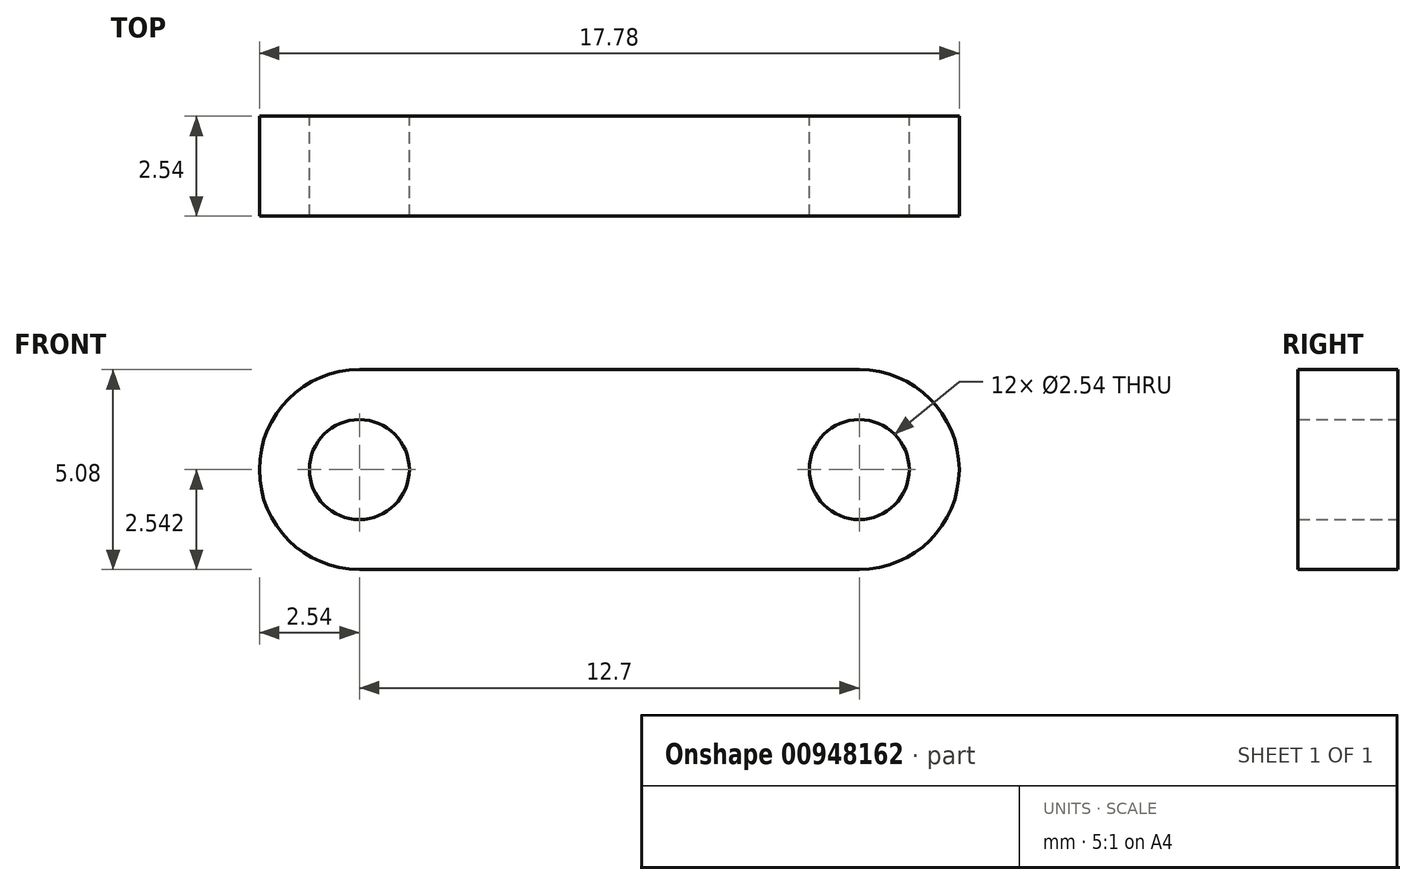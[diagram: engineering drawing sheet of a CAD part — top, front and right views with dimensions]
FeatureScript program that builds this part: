
annotation { "Feature Type Name" : "Feature", "Feature Type Description" : "" }
export const myFeature = defineFeature(function(context is Context, id is Id, definition is map)
    precondition{}
    {
        {
            var Q0;
            Q0=qCreatedBy(makeId("Front.planeOp"),FACE);
            var sketch = newSketch(context, id + "F0", { "sketchPlane" : qUnion([Q0])});
            skLineSegment(sketch, "E0.bottom", {"start": v(-11.89, 32.28) * mm, "end": v(0.81, 32.28) * mm});
            skLineSegment(sketch, "E0.top", {"start": v(-11.89, 27.2) * mm, "end": v(0.81, 27.2) * mm});
            skArc(sketch, "E1", {"start": v(-11.89, 32.28) * mm, "mid": v(-14.43, 29.74) * mm, "end": v(-11.89, 27.2) * mm});
            skArc(sketch, "E2", {"start": v(0.81, 27.2) * mm, "mid": v(3.35, 29.74) * mm, "end": v(0.81, 32.28) * mm});
            skCircle(sketch, "E3", {"center": v(-11.89, 29.74) * mm, "radius": 1.27 * mm});
            skCircle(sketch, "E4", {"center": v(0.81, 29.74) * mm, "radius": 1.27 * mm});
            skSolve(sketch);
        }
        {
            var Q0;
            Q0=makeQuery(id+"F0.imprint","IMPRINT",FACE,{"disambiguationData":[TD([[makeQuery(id+"F0.imprint","IMPRINT",EDGE,{"derivedFrom":sQuery(id+"F0.wireOp",EDGE,"E0.bottom")}),-1.0]])]});
            extrude(context, id + "F1", {"entities" : qUnion([Q0]), "depth" : 2.54 * mm, "offsetDistance" : 25.4 * mm});
        }
    });
